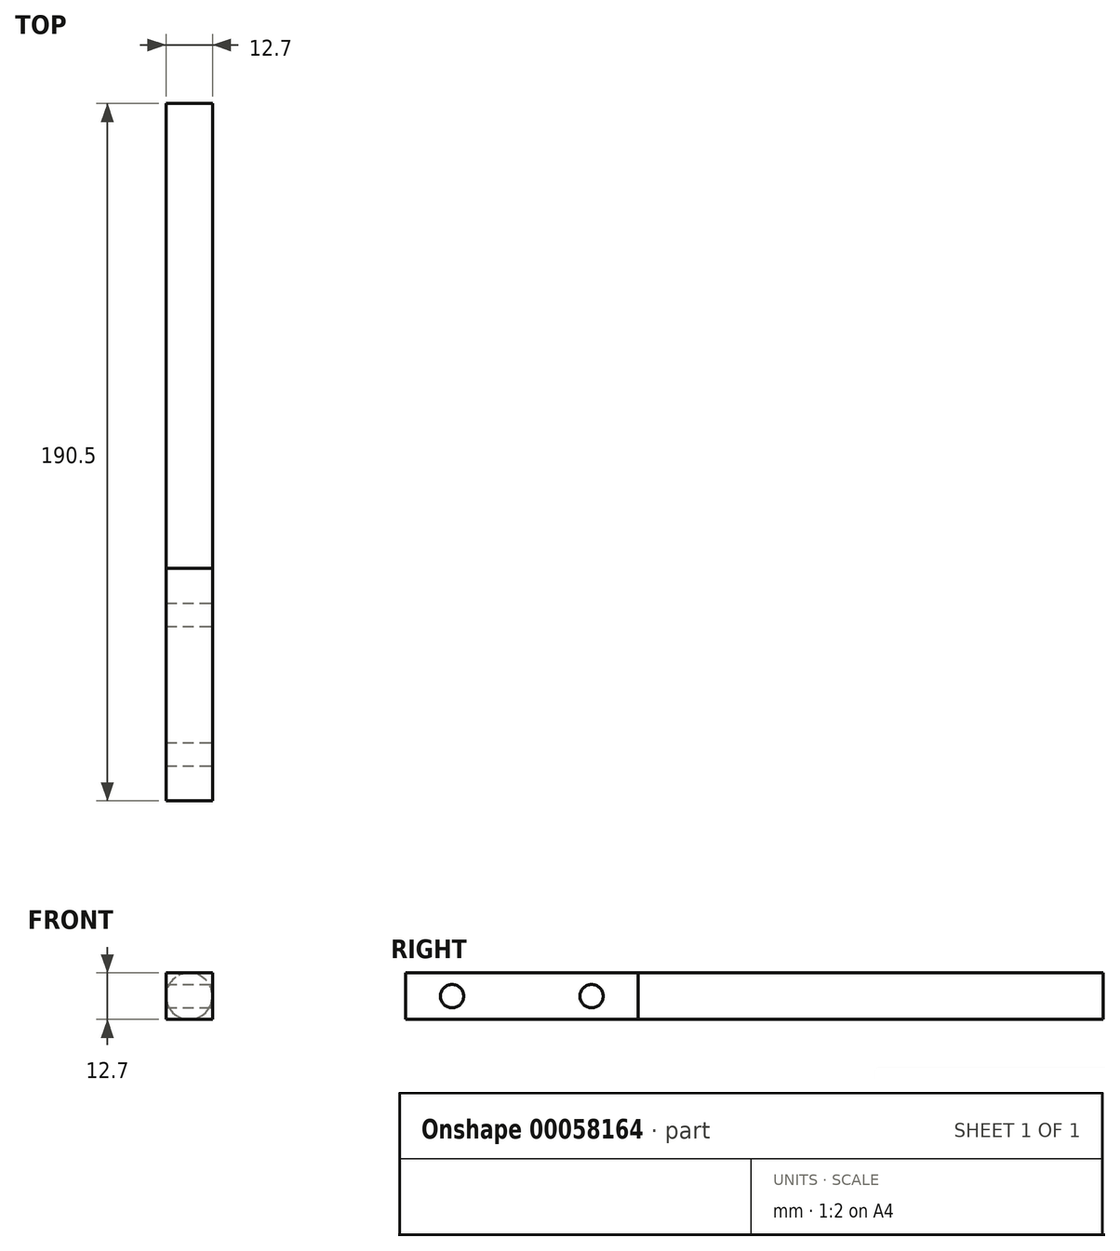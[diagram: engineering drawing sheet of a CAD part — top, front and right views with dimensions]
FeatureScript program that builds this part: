
annotation { "Feature Type Name" : "Feature", "Feature Type Description" : "" }
export const myFeature = defineFeature(function(context is Context, id is Id, definition is map)
    precondition{}
    {
        {
            var Q0;
            Q0=qCreatedBy(makeId("Front.planeOp"),FACE);
            var sketch = newSketch(context, id + "F0", { "sketchPlane" : qUnion([Q0])});
            skLineSegment(sketch, "E0.rect.bottom", {"start": v(6.35, -6.35) * mm, "end": v(-6.35, -6.35) * mm});
            skLineSegment(sketch, "E0.rect.top", {"start": v(6.35, 6.35) * mm, "end": v(-6.35, 6.35) * mm});
            skLineSegment(sketch, "E0.rect.left", {"start": v(6.35, -6.35) * mm, "end": v(6.35, 6.35) * mm});
            skLineSegment(sketch, "E0.rect.right", {"start": v(-6.35, -6.35) * mm, "end": v(-6.35, 6.35) * mm});
            skPoint(sketch, "E0.rect.middle", {"position": v(0, 0) * mm});
            skSolve(sketch);
        }
        {
            var Q0;
            Q0=makeQuery(id+"F0.imprint","IMPRINT",FACE,{"disambiguationData":[TD([[makeQuery(id+"F0.imprint","IMPRINT",EDGE,{"derivedFrom":sQuery(id+"F0.wireOp",EDGE,"E0.rect.bottom")}),-1.0]])]});
            extrude(context, id + "F1", {"entities" : qUnion([Q0]), "depth" : 63.5 * mm});
        }
        {
            var Q0;
            Q0=makeQuery(id+"F1.opExtrude","SWEPT_FACE",FACE,{"disambiguationData":[OSD([sQuery(id+"F0.wireOp",EDGE,"E0.rect.left")])]});
            var sketch = newSketch(context, id + "F2", { "sketchPlane" : qUnion([Q0])});
            skCircle(sketch, "E1", {"center": v(-50.8, 0) * mm, "radius": 3.18 * mm});
            skCircle(sketch, "E2", {"center": v(-12.7, 0) * mm, "radius": 3.18 * mm});
            skSolve(sketch);
        }
        {
            var Q0;
            Q0=makeQuery(id+"F2.imprint","IMPRINT",FACE,{"disambiguationData":[TD([[makeQuery(id+"F2.imprint","IMPRINT",EDGE,{"derivedFrom":sQuery(id+"F2.wireOp",EDGE,"E1")}),1.0]])]});
            var Q1;
            Q1=makeQuery(id+"F2.imprint","IMPRINT",FACE,{"disambiguationData":[TD([[makeQuery(id+"F2.imprint","IMPRINT",EDGE,{"derivedFrom":sQuery(id+"F2.wireOp",EDGE,"E2")}),1.0]])]});
            extrude(context, id + "F3", {"entities" : qUnion([Q0, Q1]), "operationType" : NewBodyOperationType.REMOVE, "endBound" : BoundingType.THROUGH_ALL, "oppositeDirection" : true, "depth" : 25.4 * mm});
        }
        {
            var Q0;
            Q0=makeQuery(id+"F1.opExtrude","CAP_FACE",FACE,{"disambiguationData":[OSD([sQuery(id+"F0.wireOp",EDGE,"E0.rect.bottom"),sQuery(id+"F0.wireOp",EDGE,"E0.rect.top"),sQuery(id+"F0.wireOp",EDGE,"E0.rect.left"),sQuery(id+"F0.wireOp",EDGE,"E0.rect.right")])],"isStart":true});
            var sketch = newSketch(context, id + "F4", { "sketchPlane" : qUnion([Q0])});
            skCircle(sketch, "E3", {"center": v(0, 0) * mm, "radius": 6.35 * mm});
            skSolve(sketch);
        }
        {
            var Q0;
            {var subQ0=sQuery(id+"F4.wireOp",EDGE,"E3");var subQ1=makeQuery(id+"F4.imprint","INTERSECT",VERTEX,{"derivedFrom":[makeQuery(id+"F1.opExtrude","CAP_EDGE",EDGE,{"disambiguationData":[OSD([sQuery(id+"F0.wireOp",EDGE,"E0.rect.top")])],"isStart":true}),subQ0]});Q0=makeQuery(id+"F4.imprint","IMPRINT",FACE,{"disambiguationData":[TD([[makeQuery(id+"F4.imprint","IMPRINT",EDGE,{"disambiguationData":[TD([[subQ1,1.0]])],"derivedFrom":subQ0}),1.0]])]});}
            extrude(context, id + "F5", {"entities" : qUnion([Q0]), "operationType" : NewBodyOperationType.ADD, "depth" : 127 * mm});
        }
    });
